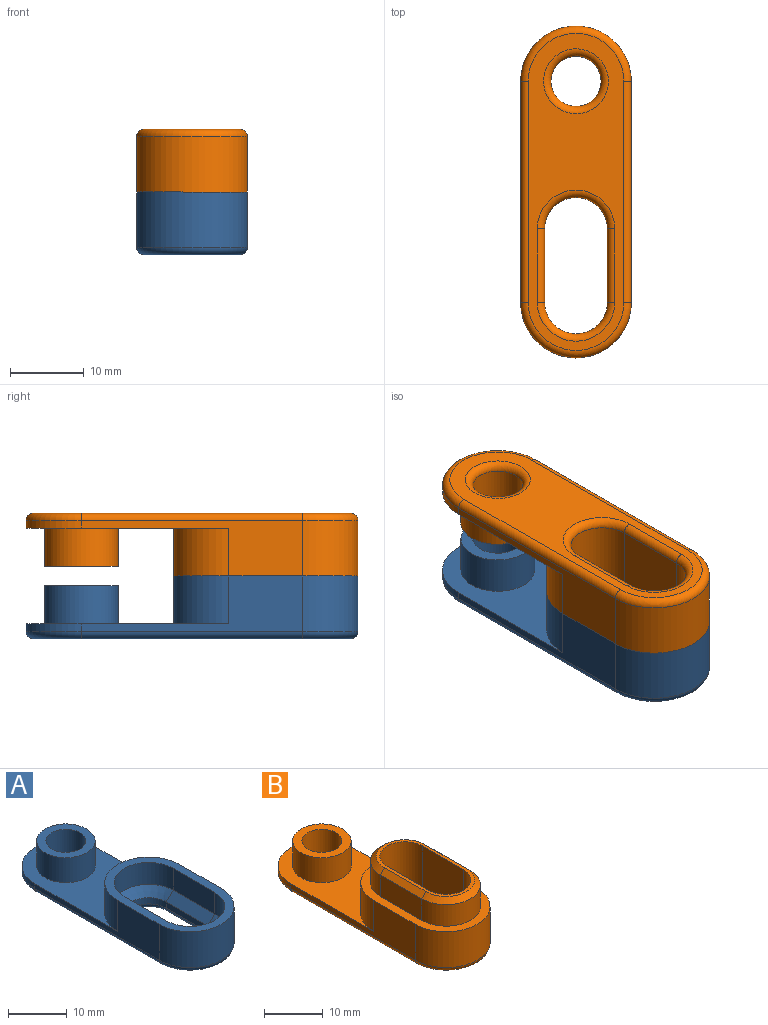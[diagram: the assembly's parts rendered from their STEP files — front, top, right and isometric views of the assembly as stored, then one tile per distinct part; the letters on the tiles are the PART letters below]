
ASSEMBLY  parts=2 mates=1
PART A: 32 faces, bbox 16.2x46.2x8.5 mm
  f0: plane 27.5x15mm, normal (0,0,1), area 221.5mm2, adj f4,f6,f8,f11,f16
  f1: cylinder r=4.25mm len=8.5mm, axis (0,0,1), area 17.4mm2, adj f2,f9,f19,f27
  f2: plane 10x1.3mm, normal (-1,0,0), area 13mm2, adj f1,f3,f21,f29
  f3: cylinder r=4.25mm len=8.5mm, axis (0,0,1), area 17.4mm2, adj f2,f9,f22,f30
  f4: plane 30x7.5mm, normal (-1,0,0), area 95mm2, adj f0,f5,f8,f16,f18,f26
  f5: cylinder r=7.5mm len=15mm, axis (0,0,1), area 176.7mm2, adj f4,f6,f18,f24
  f6: plane 30x7.5mm, normal (1,0,0), area 95mm2, adj f0,f5,f8,f16,f18,f23
  f7: cylinder r=3.4mm len=6.8mm, axis (0,0,1), area 132.4mm2, adj f12,f31
  f8: cylinder r=7.5mm len=15mm, axis (0,0,1), area 23.6mm2, adj f0,f4,f6,f25
  f9: plane 10x1.3mm, normal (1,0,0), area 13mm2, adj f1,f3,f20,f28
  f10: plane 43x13mm, normal (0,0,-1), area 270.3mm2, adj f23,f24,f25,f26,f27,f28,f29,f30
  f11: cylinder r=5mm len=10mm, axis (0,0,-1), area 163.4mm2, adj f0,f12
  f12: plane 10x10mm, normal (0,0,1), area 42.2mm2, adj f7,f11
  f13: cylinder r=5.9mm len=11.8mm, axis (0,0,-1), area 84.3mm2, adj f14,f17,f18,f19
  f14: plane 10x4.55mm, normal (-1,0,0), area 45.5mm2, adj f13,f15,f18,f21
  f15: cylinder r=5.9mm len=11.8mm, axis (0,0,-1), area 84.3mm2, adj f14,f17,f18,f22
  f16: cylinder r=7.5mm len=15mm, axis (0,0,-1), area 153.2mm2, adj f0,f4,f6,f18
  f17: plane 10x4.55mm, normal (1,0,0), area 45.5mm2, adj f13,f15,f18,f20
  f18: plane 25x15mm, normal (0,0,1), area 99.4mm2, adj f4,f5,f6,f13,f14,f15,f16,f17
  f19: cone r=4.25mm half-angle=45deg, axis (0,0,1), area 37.2mm2, adj f1,f13,f20,f21
  f20: plane 10x1.65mm, normal (0.71,0,0.71), area 23.3mm2, adj f9,f17,f19,f22
  f21: plane 10x1.65mm, normal (-0.71,0,0.71), area 23.3mm2, adj f2,f14,f19,f22
  f22: cone r=4.25mm half-angle=45deg, axis (0,0,1), area 37.2mm2, adj f3,f15,f20,f21
  f23: cylinder r=1mm len=30mm, axis (0,-1,0), area 47.1mm2, adj f6,f10,f24,f25
  f24: torus R=6.5mm, axis (0,0,1), area 35.2mm2, adj f5,f10,f23,f26
  f25: torus R=6.5mm, axis (0,0,1), area 35.2mm2, adj f8,f10,f23,f26
  f26: cylinder r=1mm len=30mm, axis (0,1,0), area 47.1mm2, adj f4,f10,f24,f25
  f27: torus R=5.25mm, axis (0,0,1), area 22.8mm2, adj f1,f10,f28,f29
  f28: cylinder r=1mm len=10mm, axis (0,-1,0), area 15.7mm2, adj f9,f10,f27,f30
  f29: cylinder r=1mm len=10mm, axis (0,1,0), area 15.7mm2, adj f2,f10,f27,f30
  f30: torus R=5.25mm, axis (0,0,1), area 22.8mm2, adj f3,f10,f28,f29
  f31: torus R=4.4mm, axis (0,0,1), area 37.1mm2, adj f7,f10
PART B: 33 faces, bbox 16.2x46.2x14 mm
  f0: plane 27.5x15mm, normal (0,0,1), area 221.5mm2, adj f4,f5,f6,f11,f13
  f1: cylinder r=4.25mm len=13mm, axis (0,0,1), area 173.6mm2, adj f2,f9,f19,f20
  f2: plane 13x10mm, normal (1,0,0), area 130mm2, adj f1,f3,f19,f22
  f3: cylinder r=4.25mm len=13mm, axis (0,0,1), area 173.6mm2, adj f2,f9,f19,f23
  f4: plane 30x7.5mm, normal (1,0,0), area 95mm2, adj f0,f5,f8,f13,f14,f27
  f5: cylinder r=7.5mm len=15mm, axis (0,0,1), area 23.6mm2, adj f0,f4,f6,f25
  f6: plane 30x7.5mm, normal (-1,0,0), area 95mm2, adj f0,f5,f8,f13,f14,f26
  f7: cylinder r=3.4mm len=6.8mm, axis (0,0,1), area 132.4mm2, adj f12,f24
  f8: cylinder r=7.5mm len=15mm, axis (0,0,1), area 176.7mm2, adj f4,f6,f14,f28
  f9: plane 13x10mm, normal (-1,0,0), area 130mm2, adj f1,f3,f19,f21
  f10: plane 43x13mm, normal (0,0,-1), area 270.3mm2, adj f20,f21,f22,f23,f24,f25,f26,f27
  f11: cylinder r=5mm len=10mm, axis (0,0,-1), area 163.4mm2, adj f0,f12
  f12: plane 10x10mm, normal (0,0,1), area 42.2mm2, adj f7,f11
  f13: cylinder r=7.5mm len=15mm, axis (0,0,-1), area 153.2mm2, adj f0,f4,f6,f14
  f14: plane 25x15mm, normal (0,0,1), area 102.2mm2, adj f4,f6,f8,f13,f15,f16,f17,f18
  f15: cylinder r=5.85mm len=11.7mm, axis (0,0,-1), area 82.7mm2, adj f14,f16,f18,f32
  f16: plane 10x4.5mm, normal (-1,0,0), area 45mm2, adj f14,f15,f17,f31
  f17: cylinder r=5.85mm len=11.7mm, axis (0,0,-1), area 82.7mm2, adj f14,f16,f18,f29
  f18: plane 10x4.5mm, normal (1,0,0), area 45mm2, adj f14,f15,f17,f30
  f19: plane 19.7x9.7mm, normal (0,0,1), area 29.2mm2, adj f1,f2,f3,f9,f29,f30,f31,f32
  f20: torus R=5.25mm, axis (0,0,1), area 22.8mm2, adj f1,f10,f21,f22
  f21: cylinder r=1mm len=10mm, axis (0,1,0), area 15.7mm2, adj f9,f10,f20,f23
  f22: cylinder r=1mm len=10mm, axis (0,-1,0), area 15.7mm2, adj f2,f10,f20,f23
  f23: torus R=5.25mm, axis (0,0,1), area 22.8mm2, adj f3,f10,f21,f22
  f24: torus R=4.4mm, axis (0,0,1), area 37.1mm2, adj f7,f10
  f25: torus R=6.5mm, axis (0,0,1), area 35.2mm2, adj f5,f10,f26,f27
  f26: cylinder r=1mm len=30mm, axis (0,1,0), area 47.1mm2, adj f6,f10,f25,f28
  f27: cylinder r=1mm len=30mm, axis (0,-1,0), area 47.1mm2, adj f4,f10,f25,f28
  f28: torus R=6.5mm, axis (0,0,1), area 35.2mm2, adj f8,f10,f26,f27
  f29: cone r=4.85mm half-angle=45deg, axis (0,0,-1), area 23.8mm2, adj f17,f19,f30,f31
  f30: plane 10x1mm, normal (0.71,0,0.71), area 14.1mm2, adj f18,f19,f29,f32
  f31: plane 10x1mm, normal (-0.71,0,0.71), area 14.1mm2, adj f16,f19,f29,f32
  f32: cone r=4.85mm half-angle=45deg, axis (0,0,-1), area 23.8mm2, adj f15,f19,f30,f31
PLACE A t=(1.9,11.1,-9.35)mm fixed
PLACE B rot(axis=(0,-1,0),180deg) t=(1.9,11.1,3.65)mm
MATE slider A.f1 <-> B.f3  axis (0,0,1) through (1.9,-8.9,-2.85)mm
